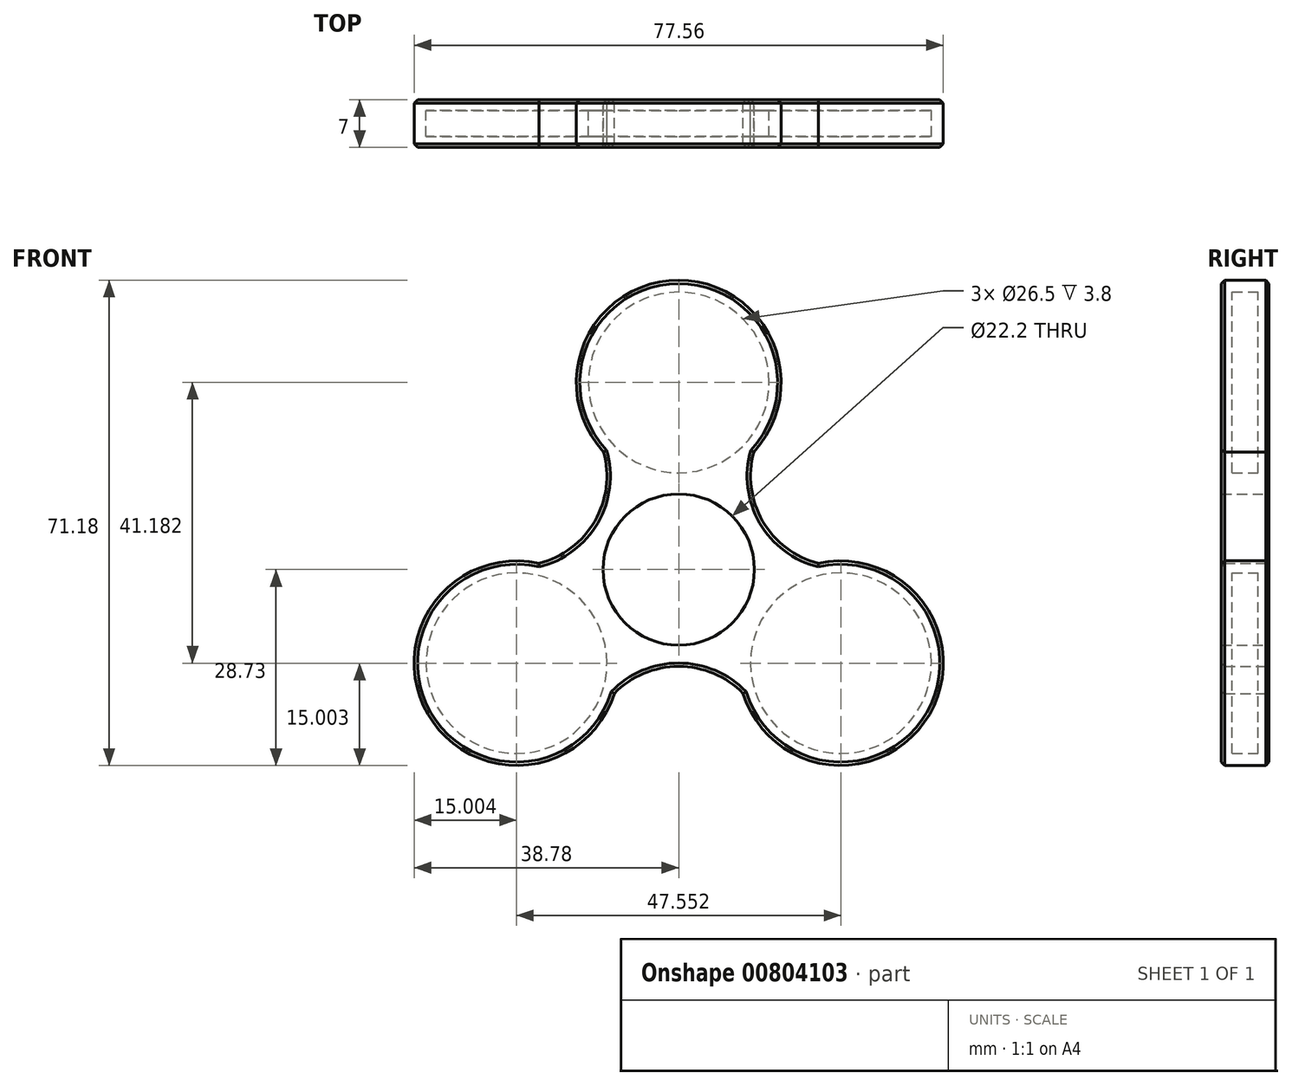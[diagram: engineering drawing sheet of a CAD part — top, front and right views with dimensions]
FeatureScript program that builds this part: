
annotation { "Feature Type Name" : "Feature", "Feature Type Description" : "" }
export const myFeature = defineFeature(function(context is Context, id is Id, definition is map)
    precondition{}
    {
        {
            var Q0;
            Q0=qCreatedBy(makeId("Front.planeOp"),FACE);
            var sketch = newSketch(context, id + "F0", { "sketchPlane" : qUnion([Q0])});
            skCircle(sketch, "E0", {"center": v(0, 0) * mm, "radius": 11.1 * mm});
            skCircle(sketch, "E1", {"center": v(0, 27.45) * mm, "radius": 13.25 * mm});
            skArc(sketch, "E2", {"start": v(11, 17.26) * mm, "mid": v(0, 42.45) * mm, "end": v(-11, 17.26) * mm});
            skArc(sketch, "E3.1.1", {"start": v(-20.45, 0.9) * mm, "mid": v(-12.3, 7.1) * mm, "end": v(-11, 17.26) * mm});
            skArc(sketch, "E3.2.0", {"start": v(-20.45, 0.9) * mm, "mid": v(-36.77, -21.23) * mm, "end": v(-9.45, -18.16) * mm});
            skCircle(sketch, "E3.2.1", {"center": v(-23.78, -13.73) * mm, "radius": 13.25 * mm});
            skArc(sketch, "E3.3.1", {"start": v(9.45, -18.16) * mm, "mid": v(0, -14.2) * mm, "end": v(-9.45, -18.16) * mm});
            skArc(sketch, "E3.4.0", {"start": v(9.45, -18.16) * mm, "mid": v(36.77, -21.23) * mm, "end": v(20.45, 0.9) * mm});
            skCircle(sketch, "E3.4.1", {"center": v(23.78, -13.73) * mm, "radius": 13.25 * mm});
            skArc(sketch, "E3.5.1", {"start": v(11, 17.26) * mm, "mid": v(12.3, 7.1) * mm, "end": v(20.45, 0.9) * mm});
            skSolve(sketch);
        }
        {
            var Q0;
            Q0=makeQuery(id+"F0.imprint","IMPRINT",FACE,{"disambiguationData":[TD([[makeQuery(id+"F0.imprint","IMPRINT",EDGE,{"derivedFrom":sQuery(id+"F0.wireOp",EDGE,"E0")}),-1.0]])]});
            extrude(context, id + "F1", {"entities" : qUnion([Q0]), "endBound" : BoundingType.SYMMETRIC, "depth" : 6 * mm, "offsetDistance" : 25 * mm});
        }
        {
            var Q0;
            Q0=makeQuery(id+"F0.imprint","IMPRINT",FACE,{"disambiguationData":[TD([[makeQuery(id+"F0.imprint","IMPRINT",EDGE,{"derivedFrom":sQuery(id+"F0.wireOp",EDGE,"E3.2.1")}),1.0]])]});
            var Q1;
            Q1=makeQuery(id+"F0.imprint","IMPRINT",FACE,{"disambiguationData":[TD([[makeQuery(id+"F0.imprint","IMPRINT",EDGE,{"derivedFrom":sQuery(id+"F0.wireOp",EDGE,"E0")}),1.0]])]});
            var Q2;
            Q2=makeQuery(id+"F0.imprint","IMPRINT",FACE,{"disambiguationData":[TD([[makeQuery(id+"F0.imprint","IMPRINT",EDGE,{"derivedFrom":sQuery(id+"F0.wireOp",EDGE,"E1")}),1.0]])]});
            var Q3;
            Q3=makeQuery(id+"F0.imprint","IMPRINT",FACE,{"disambiguationData":[TD([[makeQuery(id+"F0.imprint","IMPRINT",EDGE,{"derivedFrom":sQuery(id+"F0.wireOp",EDGE,"E3.4.1")}),1.0]])]});
            var Q4;
            Q4=makeQuery(id+"F0.imprint","IMPRINT",FACE,{"disambiguationData":[TD([[makeQuery(id+"F0.imprint","IMPRINT",EDGE,{"derivedFrom":sQuery(id+"F0.wireOp",EDGE,"E0")}),-1.0]])]});
            extrude(context, id + "F2", {"entities" : qUnion([Q0, Q1, Q2, Q3, Q4]), "operationType" : NewBodyOperationType.ADD, "depth" : 3.5 * mm, "offsetDistance" : 25 * mm, "hasSecondDirection" : true, "secondDirectionOppositeDirection" : false, "secondDirectionDepth" : 1.9 * mm});
        }
        {
            var Q0;
            Q0=makeQuery(id+"F0.imprint","IMPRINT",FACE,{"disambiguationData":[TD([[makeQuery(id+"F0.imprint","IMPRINT",EDGE,{"derivedFrom":sQuery(id+"F0.wireOp",EDGE,"E1")}),1.0]])]});
            var Q1;
            Q1=makeQuery(id+"F0.imprint","IMPRINT",FACE,{"disambiguationData":[TD([[makeQuery(id+"F0.imprint","IMPRINT",EDGE,{"derivedFrom":sQuery(id+"F0.wireOp",EDGE,"E0")}),1.0]])]});
            var Q2;
            Q2=makeQuery(id+"F0.imprint","IMPRINT",FACE,{"disambiguationData":[TD([[makeQuery(id+"F0.imprint","IMPRINT",EDGE,{"derivedFrom":sQuery(id+"F0.wireOp",EDGE,"E3.2.1")}),1.0]])]});
            var Q3;
            Q3=makeQuery(id+"F0.imprint","IMPRINT",FACE,{"disambiguationData":[TD([[makeQuery(id+"F0.imprint","IMPRINT",EDGE,{"derivedFrom":sQuery(id+"F0.wireOp",EDGE,"E3.4.1")}),1.0]])]});
            var Q4;
            Q4=makeQuery(id+"F0.imprint","IMPRINT",FACE,{"disambiguationData":[TD([[makeQuery(id+"F0.imprint","IMPRINT",EDGE,{"derivedFrom":sQuery(id+"F0.wireOp",EDGE,"E0")}),-1.0]])]});
            extrude(context, id + "F3", {"entities" : qUnion([Q0, Q1, Q2, Q3, Q4]), "operationType" : NewBodyOperationType.ADD, "oppositeDirection" : true, "depth" : 3.5 * mm, "offsetDistance" : 25 * mm, "hasSecondDirection" : true, "secondDirectionOppositeDirection" : true, "secondDirectionDepth" : 1.9 * mm});
        }
        {
            var Q0;
            Q0=makeQuery(id+"F2.opExtrude","CAP_FACE",FACE,{"disambiguationData":[OSD([sQuery(id+"F0.wireOp",EDGE,"E2"),sQuery(id+"F0.wireOp",EDGE,"E3.1.1"),sQuery(id+"F0.wireOp",EDGE,"E3.2.0"),sQuery(id+"F0.wireOp",EDGE,"E3.3.1"),sQuery(id+"F0.wireOp",EDGE,"E3.4.0"),sQuery(id+"F0.wireOp",EDGE,"E3.5.1")])],"isStart":false});
            var sketch = newSketch(context, id + "F4", { "sketchPlane" : qUnion([Q0])});
            skCircle(sketch, "E4", {"center": v(0, 0) * mm, "radius": 11.1 * mm});
            skSolve(sketch);
        }
        {
            var Q0;
            Q0=sQuery(id+"F4.wireOp",VERTEX,"E4.center");
            var Q1;
            Q1=makeQuery(id+"F1.opExtrude","SWEPT_BODY",BODY,{"disambiguationData":[OSD([sQuery(id+"F0.wireOp",EDGE,"E0"),sQuery(id+"F0.wireOp",EDGE,"E1"),sQuery(id+"F0.wireOp",EDGE,"E2"),sQuery(id+"F0.wireOp",EDGE,"E3.1.1"),sQuery(id+"F0.wireOp",EDGE,"E3.2.0"),sQuery(id+"F0.wireOp",EDGE,"E3.2.1"),sQuery(id+"F0.wireOp",EDGE,"E3.3.1"),sQuery(id+"F0.wireOp",EDGE,"E3.4.0"),sQuery(id+"F0.wireOp",EDGE,"E3.4.1"),sQuery(id+"F0.wireOp",EDGE,"E3.5.1")])]});
            hole(context, id + "F5", {"style" : HoleStyle.SIMPLE, "endStyle" : HoleEndStyle.THROUGH, "holeDiameter" : 22.2 * mm, "majorDiameter" : 5 * mm, "isTappedThrough" : true, "tappedDepth" : 12 * mm, "tapClearance" : 3, "locations" : qUnion([Q0]), "scope" : qUnion([Q1])});
        }
        {
            var Q0;
            Q0=makeQuery(id+"F2.opExtrude","CAP_EDGE",EDGE,{"disambiguationData":[OSD([sQuery(id+"F0.wireOp",EDGE,"E3.4.0")])],"isStart":false});
            var Q1;
            Q1=makeQuery(id+"F2.opExtrude","CAP_EDGE",EDGE,{"disambiguationData":[OSD([sQuery(id+"F0.wireOp",EDGE,"E3.5.1")])],"isStart":false});
            var Q2;
            Q2=makeQuery(id+"F2.opExtrude","CAP_EDGE",EDGE,{"disambiguationData":[OSD([sQuery(id+"F0.wireOp",EDGE,"E2")])],"isStart":false});
            var Q3;
            Q3=makeQuery(id+"F2.opExtrude","CAP_EDGE",EDGE,{"disambiguationData":[OSD([sQuery(id+"F0.wireOp",EDGE,"E3.1.1")])],"isStart":false});
            var Q4;
            Q4=makeQuery(id+"F5.hole-0.boolean.opBoolean","COPY",EDGE,{"derivedFrom":makeQuery(id+"F5.hole-0.opRevolve","SWEPT_EDGE",EDGE,{"disambiguationData":[OSD([sQuery(id+"F5.hole-0.sketch.wireOp",EDGE,"core_line_2"),sQuery(id+"F5.hole-0.sketch.wireOp",EDGE,"core_line_3")])]})});
            var Q5;
            Q5=makeQuery(id+"F5.hole-0.boolean.opBoolean","INTERSECT",EDGE,{"derivedFrom":[makeQuery(id+"F3.opExtrude","CAP_FACE",FACE,{"disambiguationData":[OSD([sQuery(id+"F0.wireOp",EDGE,"E2"),sQuery(id+"F0.wireOp",EDGE,"E3.1.1"),sQuery(id+"F0.wireOp",EDGE,"E3.2.0"),sQuery(id+"F0.wireOp",EDGE,"E3.3.1"),sQuery(id+"F0.wireOp",EDGE,"E3.4.0"),sQuery(id+"F0.wireOp",EDGE,"E3.5.1")])],"isStart":false}),makeQuery(id+"F5.hole-0.opRevolve","SWEPT_FACE",FACE,{"disambiguationData":[OSD([sQuery(id+"F5.hole-0.sketch.wireOp",EDGE,"core_line_2")])]})]});
            var Q6;
            Q6=makeQuery(id+"F2.opExtrude","CAP_EDGE",EDGE,{"disambiguationData":[OSD([sQuery(id+"F0.wireOp",EDGE,"E3.3.1")])],"isStart":false});
            var Q7;
            Q7=makeQuery(id+"F2.opExtrude","CAP_EDGE",EDGE,{"disambiguationData":[OSD([sQuery(id+"F0.wireOp",EDGE,"E3.2.0")])],"isStart":false});
            var Q8;
            Q8=makeQuery(id+"F3.opExtrude","CAP_EDGE",EDGE,{"disambiguationData":[OSD([sQuery(id+"F0.wireOp",EDGE,"E3.2.0")])],"isStart":false});
            var Q9;
            Q9=makeQuery(id+"F3.opExtrude","CAP_EDGE",EDGE,{"disambiguationData":[OSD([sQuery(id+"F0.wireOp",EDGE,"E3.1.1")])],"isStart":false});
            var Q10;
            Q10=makeQuery(id+"F3.opExtrude","CAP_EDGE",EDGE,{"disambiguationData":[OSD([sQuery(id+"F0.wireOp",EDGE,"E2")])],"isStart":false});
            var Q11;
            Q11=makeQuery(id+"F3.opExtrude","CAP_EDGE",EDGE,{"disambiguationData":[OSD([sQuery(id+"F0.wireOp",EDGE,"E3.5.1")])],"isStart":false});
            var Q12;
            Q12=makeQuery(id+"F3.opExtrude","CAP_EDGE",EDGE,{"disambiguationData":[OSD([sQuery(id+"F0.wireOp",EDGE,"E3.4.0")])],"isStart":false});
            var Q13;
            Q13=makeQuery(id+"F3.opExtrude","CAP_EDGE",EDGE,{"disambiguationData":[OSD([sQuery(id+"F0.wireOp",EDGE,"E3.3.1")])],"isStart":false});
            chamfer(context, id + "F6", {"entities" : qUnion([Q0, Q1, Q2, Q3, Q4, Q5, Q6, Q7, Q8, Q9, Q10, Q11, Q12, Q13]), "width" : .5 * mm, "tangentPropagation" : true});
        }
    });
